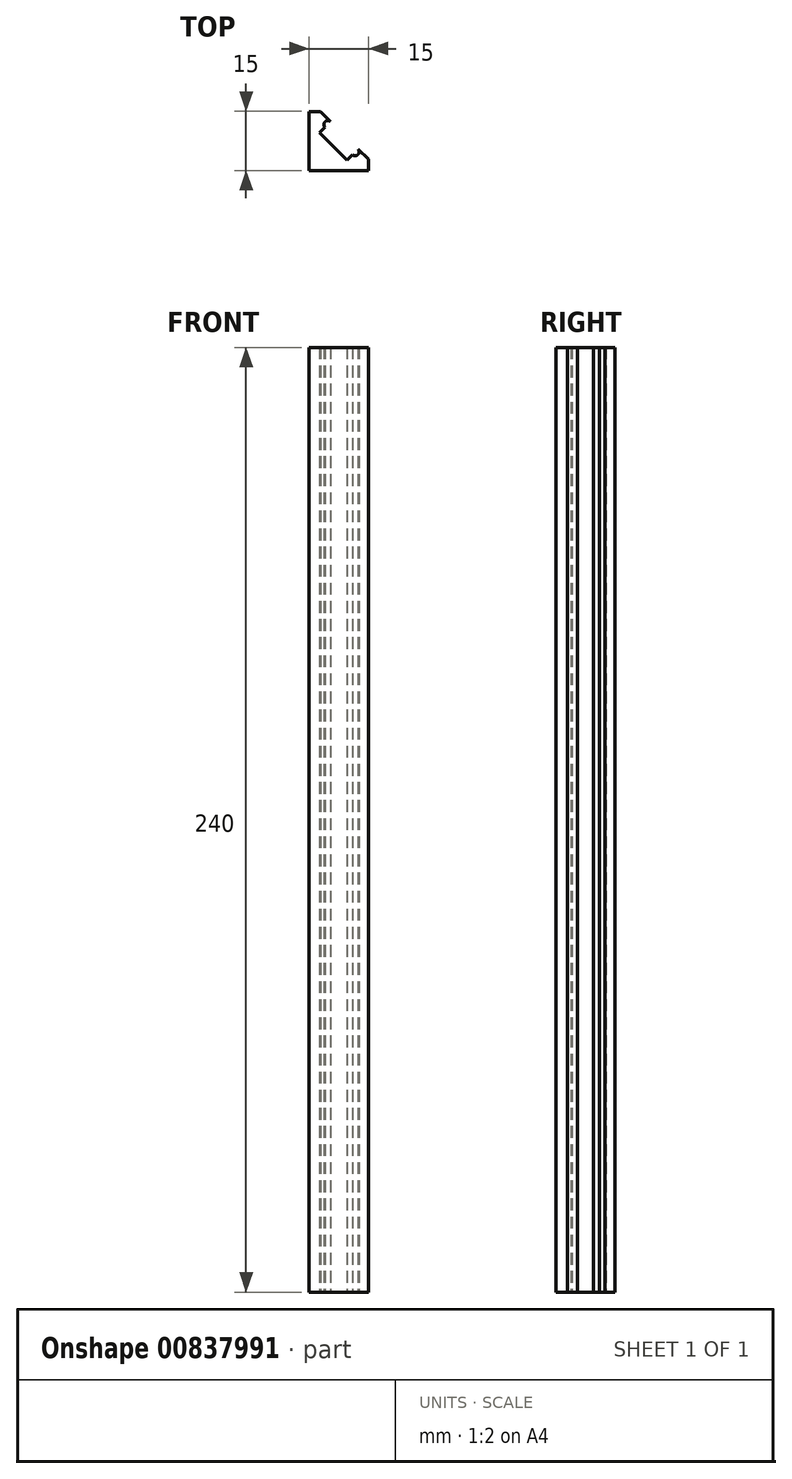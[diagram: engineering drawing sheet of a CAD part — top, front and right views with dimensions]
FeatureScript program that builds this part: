
annotation { "Feature Type Name" : "Feature", "Feature Type Description" : "" }
export const myFeature = defineFeature(function(context is Context, id is Id, definition is map)
    precondition{}
    {
        {
            var Q0;
            Q0=qCreatedBy(makeId("Top.planeOp"),FACE);
            var sketch = newSketch(context, id + "F0", { "sketchPlane" : qUnion([Q0])});
            skLineSegment(sketch, "E0.bottom", {"start": v(-7.46, -7.58) * mm, "end": v(7.54, -7.58) * mm});
            skLineSegment(sketch, "E0.top", {"start": v(-7.46, 7.42) * mm, "end": v(7.54, 7.42) * mm});
            skLineSegment(sketch, "E0.left", {"start": v(-7.46, -7.58) * mm, "end": v(-7.46, 7.42) * mm});
            skLineSegment(sketch, "E0.right", {"start": v(7.54, -7.58) * mm, "end": v(7.54, 7.42) * mm});
            skLineSegment(sketch, "E1", {"start": v(-7.46, 7.42) * mm, "end": v(7.54, -7.58) * mm});
            skLineSegment(sketch, "E2.0", {"start": v(-6.05, 8.83) * mm, "end": v(8.95, -6.17) * mm});
            skLineSegment(sketch, "E3.0", {"start": v(-8.88, 6) * mm, "end": v(6.12, -9) * mm});
            skLineSegment(sketch, "E4", {"start": v(-7.46, -7.58) * mm, "end": v(7.54, 7.42) * mm});
            skLineSegment(sketch, "E5.0", {"start": v(-10.93, -4.12) * mm, "end": v(4.07, 10.88) * mm});
            skLineSegment(sketch, "E6.0", {"start": v(-4, -11.05) * mm, "end": v(11, 3.95) * mm});
            skLineSegment(sketch, "E7", {"start": v(-3.43, 3.38) * mm, "end": v(-2.01, 4.8) * mm});
            skLineSegment(sketch, "E8", {"start": v(-2.01, 4.8) * mm, "end": v(-3.43, 3.38) * mm});
            skCircle(sketch, "E9", {"center": v(-2.72, 4.09) * mm, "radius": 1 * mm});
            skLineSegment(sketch, "E10", {"start": v(3.5, -3.55) * mm, "end": v(4.92, -2.13) * mm});
            skLineSegment(sketch, "E11", {"start": v(4.92, -2.13) * mm, "end": v(3.5, -3.55) * mm});
            skCircle(sketch, "E12", {"center": v(4.2, -2.84) * mm, "radius": 1 * mm});
            skSolve(sketch);
        }
        {
            var Q0;
            {var subQ0=sQuery(id+"F0.wireOp",EDGE,"E11");Q0=makeQuery(id+"F0.imprint","IMPRINT",FACE,{"disambiguationData":[TD([[makeQuery(id+"F0.imprint","IMPRINT",EDGE,{"derivedFrom":subQ0}),-1.0]])]});}
            var Q1;
            {var subQ1=sQuery(id+"F0.wireOp",EDGE,"E0.right");var subQ3=sQuery(id+"F0.wireOp",EDGE,"E2.0");var subQ4=makeQuery(id+"F0.imprint","INTERSECT",VERTEX,{"derivedFrom":[subQ1,subQ3]});Q1=makeQuery(id+"F0.imprint","IMPRINT",FACE,{"disambiguationData":[TD([[makeQuery(id+"F0.imprint","IMPRINT",EDGE,{"disambiguationData":[TD([[subQ4,1.0]])],"derivedFrom":subQ1}),1.0]])]});}
            var Q2;
            {var subQ0=sQuery(id+"F0.wireOp",EDGE,"E11");Q2=makeQuery(id+"F0.imprint","IMPRINT",FACE,{"disambiguationData":[TD([[makeQuery(id+"F0.imprint","IMPRINT",EDGE,{"derivedFrom":subQ0}),1.0]])]});}
            var Q3;
            {var subQ1=sQuery(id+"F0.wireOp",EDGE,"E0.bottom");var subQ3=sQuery(id+"F0.wireOp",EDGE,"E3.0");var subQ4=makeQuery(id+"F0.imprint","INTERSECT",VERTEX,{"derivedFrom":[subQ1,subQ3]});Q3=makeQuery(id+"F0.imprint","IMPRINT",FACE,{"disambiguationData":[TD([[makeQuery(id+"F0.imprint","IMPRINT",EDGE,{"disambiguationData":[TD([[subQ4,1.0]])],"derivedFrom":subQ3}),1.0]])]});}
            var Q4;
            {var subQ0=sQuery(id+"F0.wireOp",EDGE,"E6.0");var subQ1=sQuery(id+"F0.wireOp",EDGE,"E0.bottom");var subQ2=makeQuery(id+"F0.imprint","INTERSECT",VERTEX,{"derivedFrom":[subQ1,subQ0]});Q4=makeQuery(id+"F0.imprint","IMPRINT",FACE,{"disambiguationData":[TD([[makeQuery(id+"F0.imprint","IMPRINT",EDGE,{"disambiguationData":[TD([[subQ2,-1.0]])],"derivedFrom":subQ1}),1.0]])]});}
            var Q5;
            {var subQ0=sQuery(id+"F0.wireOp",EDGE,"E4");var subQ5=sQuery(id+"F0.wireOp",EDGE,"E3.0");var subQ6=makeQuery(id+"F0.imprint","INTERSECT",VERTEX,{"derivedFrom":[subQ5,subQ0]});Q5=makeQuery(id+"F0.imprint","IMPRINT",FACE,{"disambiguationData":[TD([[makeQuery(id+"F0.imprint","IMPRINT",EDGE,{"disambiguationData":[TD([[subQ6,-1.0]])],"derivedFrom":subQ5}),-1.0]])]});}
            var Q6;
            {var subQ0=sQuery(id+"F0.wireOp",EDGE,"E8");Q6=makeQuery(id+"F0.imprint","IMPRINT",FACE,{"disambiguationData":[TD([[makeQuery(id+"F0.imprint","IMPRINT",EDGE,{"derivedFrom":subQ0}),1.0]])]});}
            var Q7;
            {var subQ0=sQuery(id+"F0.wireOp",EDGE,"E8");Q7=makeQuery(id+"F0.imprint","IMPRINT",FACE,{"disambiguationData":[TD([[makeQuery(id+"F0.imprint","IMPRINT",EDGE,{"derivedFrom":subQ0}),-1.0]])]});}
            var Q8;
            {var subQ1=sQuery(id+"F0.wireOp",EDGE,"E0.left");var subQ3=sQuery(id+"F0.wireOp",EDGE,"E3.0");var subQ4=makeQuery(id+"F0.imprint","INTERSECT",VERTEX,{"derivedFrom":[subQ1,subQ3]});Q8=makeQuery(id+"F0.imprint","IMPRINT",FACE,{"disambiguationData":[TD([[makeQuery(id+"F0.imprint","IMPRINT",EDGE,{"disambiguationData":[TD([[subQ4,-1.0]])],"derivedFrom":subQ3}),1.0]])]});}
            var Q9;
            {var subQ0=sQuery(id+"F0.wireOp",EDGE,"E5.0");var subQ1=sQuery(id+"F0.wireOp",EDGE,"E0.left");var subQ2=makeQuery(id+"F0.imprint","INTERSECT",VERTEX,{"derivedFrom":[subQ1,subQ0]});Q9=makeQuery(id+"F0.imprint","IMPRINT",FACE,{"disambiguationData":[TD([[makeQuery(id+"F0.imprint","IMPRINT",EDGE,{"disambiguationData":[TD([[subQ2,-1.0]])],"derivedFrom":subQ1}),-1.0]])]});}
            var Q10;
            {var subQ3=sQuery(id+"F0.wireOp",EDGE,"E5.0");var subQ5=sQuery(id+"F0.wireOp",EDGE,"E3.0");var subQ6=makeQuery(id+"F0.imprint","INTERSECT",VERTEX,{"derivedFrom":[subQ5,subQ3]});Q10=makeQuery(id+"F0.imprint","IMPRINT",FACE,{"disambiguationData":[TD([[makeQuery(id+"F0.imprint","IMPRINT",EDGE,{"disambiguationData":[TD([[subQ6,-1.0]])],"derivedFrom":subQ5}),-1.0]])]});}
            var Q11;
            {var subQ1=sQuery(id+"F0.wireOp",EDGE,"E0.top");var subQ3=sQuery(id+"F0.wireOp",EDGE,"E2.0");var subQ4=makeQuery(id+"F0.imprint","INTERSECT",VERTEX,{"derivedFrom":[subQ1,subQ3]});Q11=makeQuery(id+"F0.imprint","IMPRINT",FACE,{"disambiguationData":[TD([[makeQuery(id+"F0.imprint","IMPRINT",EDGE,{"disambiguationData":[TD([[subQ4,1.0]])],"derivedFrom":subQ1}),-1.0]])]});}
            extrude(context, id + "F1", {"entities" : qUnion([Q0, Q1, Q2, Q3, Q4, Q5, Q6, Q7, Q8, Q9, Q10, Q11]), "depth" : 240 * mm, "offsetDistance" : 25 * mm});
        }
    });
